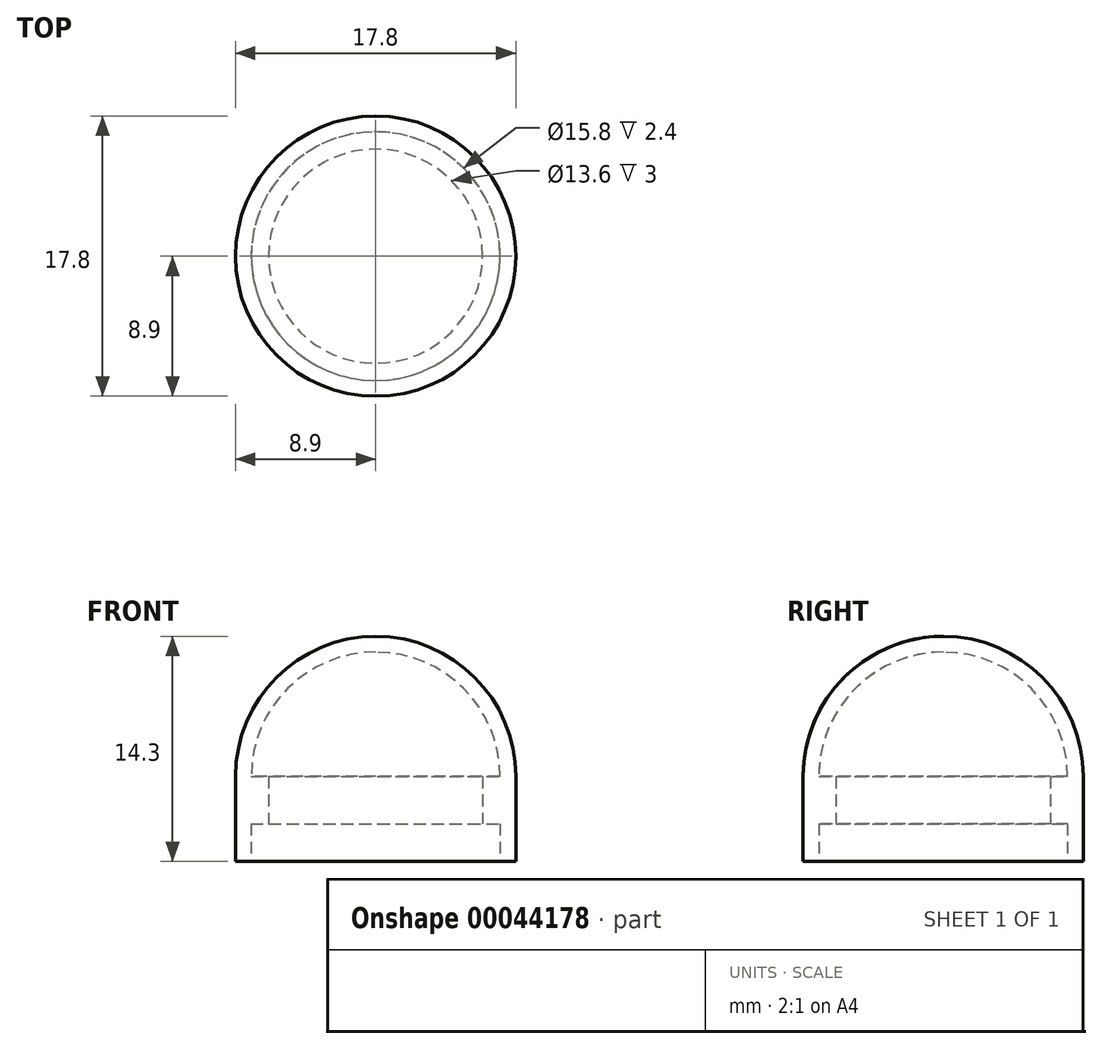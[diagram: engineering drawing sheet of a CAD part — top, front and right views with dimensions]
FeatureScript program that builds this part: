
annotation { "Feature Type Name" : "Feature", "Feature Type Description" : "" }
export const myFeature = defineFeature(function(context is Context, id is Id, definition is map)
    precondition{}
    {
        {
            var Q0;
            Q0=qCreatedBy(makeId("Top.planeOp"),FACE);
            var sketch = newSketch(context, id + "F0", { "sketchPlane" : qUnion([Q0])});
            skLineSegment(sketch, "E0", {"start": v(-17.52, 0) * mm, "end": v(42.68, 0) * mm, "construction": true});
            skLineSegment(sketch, "E1", {"start": v(0, 0) * mm, "end": v(0, 7.9) * mm, "construction": true});
            skLineSegment(sketch, "E2", {"start": v(0, 7.9) * mm, "end": v(2.4, 7.9) * mm});
            skLineSegment(sketch, "E3", {"start": v(2.4, 6.8) * mm, "end": v(2.4, 7.9) * mm});
            skLineSegment(sketch, "E4", {"start": v(2.4, 6.8) * mm, "end": v(5.4, 6.8) * mm});
            skLineSegment(sketch, "E5", {"start": v(0, 7.9) * mm, "end": v(0, 8.9) * mm});
            skLineSegment(sketch, "E6", {"start": v(5.4, 6.8) * mm, "end": v(5.4, 7.9) * mm});
            skLineSegment(sketch, "E7", {"start": v(0, 8.9) * mm, "end": v(5.4, 8.9) * mm});
            skArc(sketch, "E8", {"start": v(5.4, 8.9) * mm, "mid": v(11.7, 6.3) * mm, "end": v(14.3, 0) * mm});
            skLineSegment(sketch, "E9", {"start": v(2.4, 7.9) * mm, "end": v(5.4, 7.9) * mm, "construction": true});
            skArc(sketch, "E10", {"start": v(5.4, 7.9) * mm, "mid": v(10.99, 5.59) * mm, "end": v(13.3, 0) * mm});
            skLineSegment(sketch, "E11", {"start": v(13.3, 0) * mm, "end": v(14.3, 0) * mm});
            skSolve(sketch);
        }
        {
            var Q0;
            Q0=makeQuery(id+"F0.imprint","IMPRINT",FACE,{"disambiguationData":[TD([[makeQuery(id+"F0.imprint","IMPRINT",EDGE,{"derivedFrom":sQuery(id+"F0.wireOp",EDGE,"E2")}),1.0]])]});
            var Q1;
            Q1=sQuery(id+"F0.wireOp",EDGE,"E0");
            revolve(context, id + "F1", {"entities" : qUnion([Q0]), "axis" : qUnion([Q1]), "revolveType" : RevolveType.FULL});
        }
        {
            var Q0;
            Q0=qCreatedBy(makeId("Front.planeOp"),FACE);
            var sketch = newSketch(context, id + "F2", { "sketchPlane" : qUnion([Q0])});
            skCircle(sketch, "E12", {"center": v(0, 0) * mm, "radius": 5.01 * mm});
            skSolve(sketch);
        }
        {
            var Q0;
            Q0=makeQuery(id+"F1.opRevolve","SWEPT_BODY",BODY,{"disambiguationData":[OSD([sQuery(id+"F0.wireOp",EDGE,"E2"),sQuery(id+"F0.wireOp",EDGE,"E3"),sQuery(id+"F0.wireOp",EDGE,"E4"),sQuery(id+"F0.wireOp",EDGE,"E5"),sQuery(id+"F0.wireOp",EDGE,"E6"),sQuery(id+"F0.wireOp",EDGE,"E7"),sQuery(id+"F0.wireOp",EDGE,"E8"),sQuery(id+"F0.wireOp",EDGE,"E10"),sQuery(id+"F0.wireOp",EDGE,"E11")])]});
            var Q1;
            Q1=sQuery(id+"F2.wireOp",EDGE,"E12");
            transform(context, id + "F3", {"entities" : qUnion([Q0]), "transformType" : TransformType.ROTATION, "transformAxis" : qUnion([Q1]), "angle" : 90 * degree, "makeCopy" : false});
        }
    });
